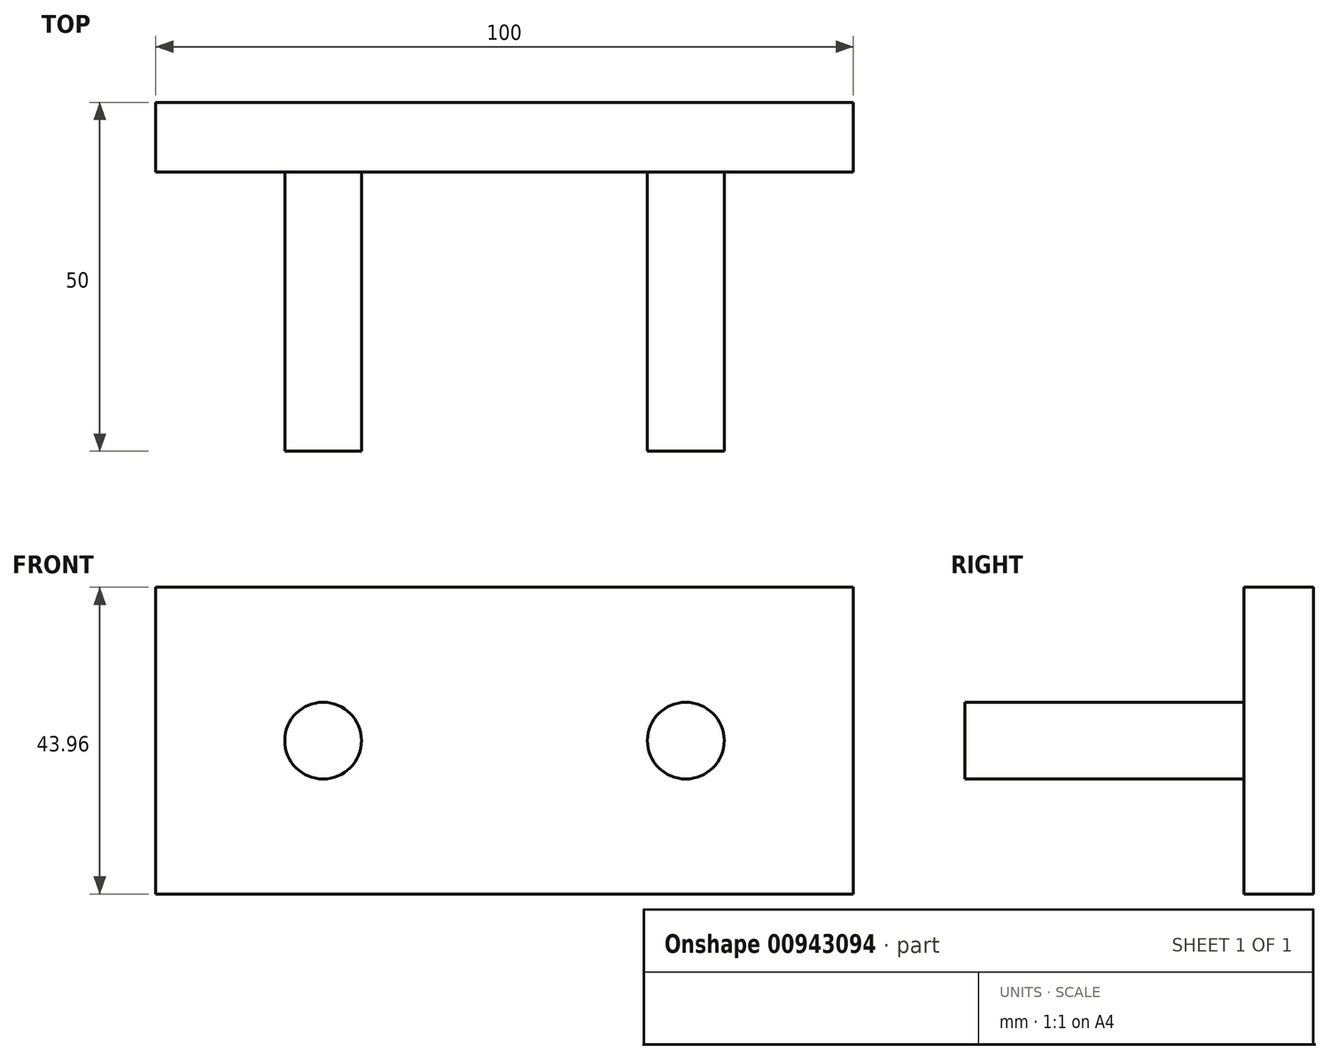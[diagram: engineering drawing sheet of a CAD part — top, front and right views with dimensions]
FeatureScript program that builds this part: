
annotation { "Feature Type Name" : "Feature", "Feature Type Description" : "" }
export const myFeature = defineFeature(function(context is Context, id is Id, definition is map)
    precondition{}
    {
        {
            var Q0;
            Q0=qCreatedBy(makeId("Front.planeOp"),FACE);
            var sketch = newSketch(context, id + "F0", { "sketchPlane" : qUnion([Q0])});
            skLineSegment(sketch, "E0.bottom", {"start": v(50, 21.98) * mm, "end": v(-50, 21.98) * mm});
            skLineSegment(sketch, "E0.top", {"start": v(50, -21.98) * mm, "end": v(-50, -21.98) * mm});
            skLineSegment(sketch, "E0.left", {"start": v(50, 21.98) * mm, "end": v(50, -21.98) * mm});
            skLineSegment(sketch, "E0.right", {"start": v(-50, 21.98) * mm, "end": v(-50, -21.98) * mm});
            skPoint(sketch, "E0.middle", {"position": v(0, 0) * mm});
            skCircle(sketch, "E1", {"center": v(-26, 0) * mm, "radius": 5.5 * mm});
            skCircle(sketch, "E2", {"center": v(26, 0) * mm, "radius": 5.5 * mm});
            skLineSegment(sketch, "E3", {"start": v(26, 0) * mm, "end": v(0, 0) * mm, "construction": true});
            skLineSegment(sketch, "E4", {"start": v(-26, 0) * mm, "end": v(0, 0) * mm, "construction": true});
            skSolve(sketch);
        }
        {
            var Q0;
            Q0=makeQuery(id+"F0.imprint","IMPRINT",FACE,{"disambiguationData":[TD([[makeQuery(id+"F0.imprint","IMPRINT",EDGE,{"derivedFrom":sQuery(id+"F0.wireOp",EDGE,"E0.bottom")}),1.0]])]});
            extrude(context, id + "F1", {"entities" : qUnion([Q0]), "depth" : 10 * mm, "offsetDistance" : 25 * mm});
        }
        {
            var Q0;
            Q0=makeQuery(id+"F0.imprint","IMPRINT",FACE,{"disambiguationData":[TD([[makeQuery(id+"F0.imprint","IMPRINT",EDGE,{"derivedFrom":sQuery(id+"F0.wireOp",EDGE,"E1")}),1.0]])]});
            var Q1;
            Q1=makeQuery(id+"F0.imprint","IMPRINT",FACE,{"disambiguationData":[TD([[makeQuery(id+"F0.imprint","IMPRINT",EDGE,{"derivedFrom":sQuery(id+"F0.wireOp",EDGE,"E2")}),1.0]])]});
            extrude(context, id + "F2", {"entities" : qUnion([Q0, Q1]), "operationType" : NewBodyOperationType.ADD, "depth" : 50 * mm, "offsetDistance" : 25 * mm});
        }
    });
